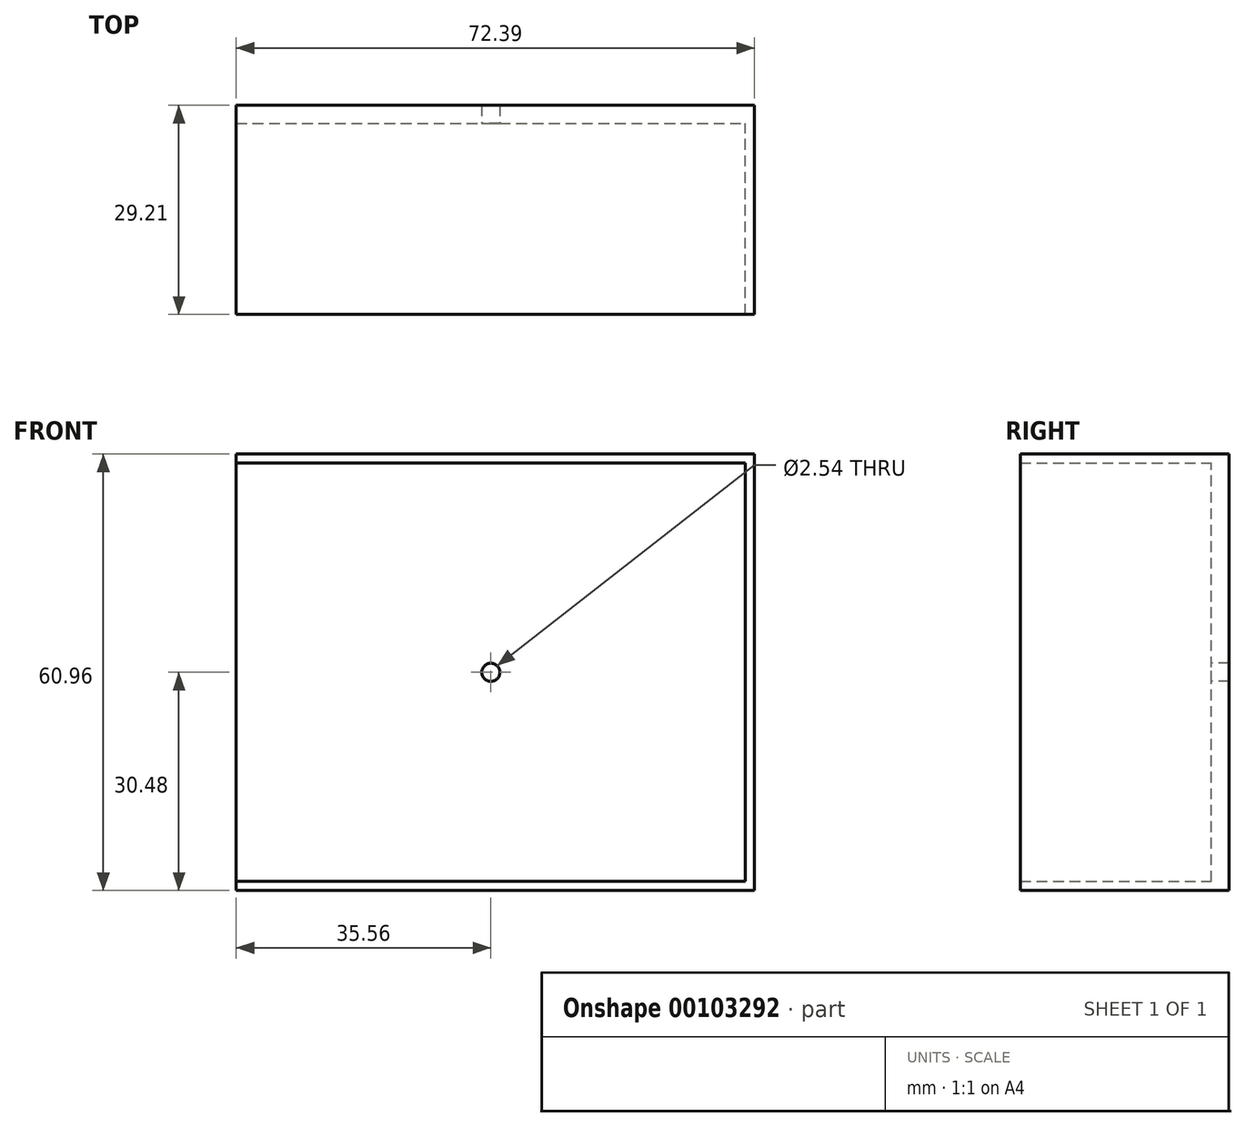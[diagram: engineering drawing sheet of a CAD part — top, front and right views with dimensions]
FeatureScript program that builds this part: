
annotation { "Feature Type Name" : "Feature", "Feature Type Description" : "" }
export const myFeature = defineFeature(function(context is Context, id is Id, definition is map)
    precondition{}
    {
        {
            var Q0;
            Q0=qCreatedBy(makeId("Front.planeOp"),FACE);
            var sketch = newSketch(context, id + "F0", { "sketchPlane" : qUnion([Q0])});
            skLineSegment(sketch, "E0.bottom", {"start": v(0, 0) * mm, "end": v(71.12, 0) * mm});
            skLineSegment(sketch, "E0.top", {"start": v(0, 58.42) * mm, "end": v(71.12, 58.42) * mm});
            skLineSegment(sketch, "E0.left", {"start": v(0, 0) * mm, "end": v(0, 58.42) * mm});
            skLineSegment(sketch, "E0.right", {"start": v(71.12, 0) * mm, "end": v(71.12, 58.42) * mm});
            skLineSegment(sketch, "E1.top", {"start": v(0, -1.27) * mm, "end": v(71.12, -1.27) * mm});
            skLineSegment(sketch, "E1.left", {"start": v(0, 0) * mm, "end": v(0, -1.27) * mm});
            skLineSegment(sketch, "E1.right", {"start": v(71.12, 0) * mm, "end": v(71.12, -1.27) * mm});
            skLineSegment(sketch, "E2.bottom", {"start": v(71.12, 58.42) * mm, "end": v(0, 58.42) * mm});
            skLineSegment(sketch, "E2.top", {"start": v(71.12, 59.7) * mm, "end": v(0, 59.69) * mm});
            skLineSegment(sketch, "E2.left", {"start": v(71.12, 58.42) * mm, "end": v(71.12, 59.7) * mm});
            skLineSegment(sketch, "E2.right", {"start": v(0, 58.42) * mm, "end": v(0, 59.69) * mm});
            skLineSegment(sketch, "E3.bottom", {"start": v(71.12, 59.7) * mm, "end": v(72.4, 59.7) * mm});
            skLineSegment(sketch, "E3.top", {"start": v(71.12, -1.27) * mm, "end": v(72.4, -1.27) * mm});
            skLineSegment(sketch, "E3.left", {"start": v(71.12, 59.7) * mm, "end": v(71.12, -1.27) * mm});
            skLineSegment(sketch, "E3.right", {"start": v(72.4, 59.7) * mm, "end": v(72.4, -1.27) * mm});
            skSolve(sketch);
        }
        {
            var Q0;
            Q0 = qSketchRegion(id + "F0", true);
            extrude(context, id + "F1", {"entities" : qUnion([Q0]), "depth" : 29.2 * mm});
        }
        {
            var Q0;
            Q0=makeQuery(id+"F0.imprint","IMPRINT",FACE,{"disambiguationData":[TD([[makeQuery(id+"F0.imprint","IMPRINT",EDGE,{"derivedFrom":sQuery(id+"F0.wireOp",EDGE,"E0.left")}),-1.0]])]});
            extrude(context, id + "F2", {"entities" : qUnion([Q0]), "operationType" : NewBodyOperationType.REMOVE, "endBound" : BoundingType.THROUGH_ALL, "depth" : 25.4 * mm});
        }
        {
            var Q0;
            Q0=makeQuery(id+"F0.imprint","IMPRINT",FACE,{"disambiguationData":[TD([[makeQuery(id+"F0.imprint","IMPRINT",EDGE,{"derivedFrom":sQuery(id+"F0.wireOp",EDGE,"E0.left")}),-1.0]])]});
            extrude(context, id + "F3", {"entities" : qUnion([Q0]), "operationType" : NewBodyOperationType.ADD, "depth" : 2.54 * mm});
        }
        {
            var Q0;
            Q0=makeQuery(id+"F3.opExtrude","CAP_FACE",FACE,{"disambiguationData":[OSD([sQuery(id+"F0.wireOp",EDGE,"E0.left"),sQuery(id+"F0.wireOp",EDGE,"E0.bottom"),sQuery(id+"F0.wireOp",EDGE,"E2.bottom"),sQuery(id+"F0.wireOp",EDGE,"E3.left")])],"isStart":false});
            var sketch = newSketch(context, id + "F4", { "sketchPlane" : qUnion([Q0])});
            skPoint(sketch, "E4", {"position": v(35.56, 29.21) * mm});
            skCircle(sketch, "E5", {"center": v(35.56, 29.21) * mm, "radius": 1.27 * mm});
            skSolve(sketch);
        }
        {
            var Q0;
            Q0=makeQuery(id+"F4.imprint","IMPRINT",FACE,{"disambiguationData":[TD([[makeQuery(id+"F4.imprint","IMPRINT",EDGE,{"derivedFrom":sQuery(id+"F4.wireOp",EDGE,"E5")}),1.0]])]});
            extrude(context, id + "F5", {"entities" : qUnion([Q0]), "operationType" : NewBodyOperationType.REMOVE, "endBound" : BoundingType.THROUGH_ALL, "oppositeDirection" : true, "depth" : 25.4 * mm});
        }
    });
